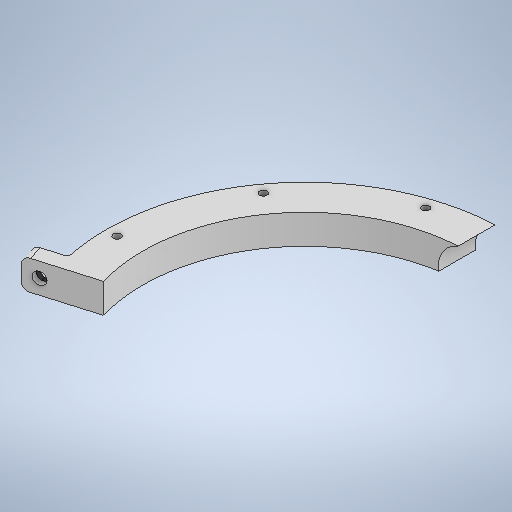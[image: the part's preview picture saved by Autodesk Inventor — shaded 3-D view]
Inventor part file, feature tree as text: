
AUTODESK INVENTOR PART (.ipt)
format: ipt  version: 2025 (Build 290162000, 162)  size: 368,640 bytes
history: native  units: in
note: dims shown in document units (in); Inventor stores cm internally (conversion verified against a paired STEP export)
features: sketch x11, extrude x8, hole x2, projected_geometry x2, fillet x1
ambient origin geometry x8: Origin, YZ Plane, XZ Plane, XY Plane, X Axis, Y Axis, Z Axis, Center Point
bodies: Solid1 (feature_tree)
feature tree (24):
  extrude  "Extrusion1"  Depth=10.6299in
  extrude  "Extrusion2"  Depth=1.4173in
  hole  "Hole1"  [1 undecoded]
  extrude  "Extrusion3"  Depth=0.1575in TaperAngle=360.0deg
  extrude  "Extrusion7"  Depth=0.1575in TaperAngle=0.0deg
  extrude  "Extrusion8"  Depth=2.7559in
  extrude  "Extrusion9"  Depth=0.7874in
  extrude  "Extrusion10"  TaperAngle=0.0deg  [1 undecoded]
  fillet  "Fillet1"  [1 undecoded]
  extrude  "Extrusion11"  Depth=0.7874in
  hole  "Hole2"  [1 undecoded]
  sketch  "Sketch1"  dims[d0=10.6299in d1=8.6614in]
  sketch  "Sketch2"  dims[d5=0.0in d6=0.0in d7=10.0394in]
  sketch  "Sketch3"  dims[d8=0.1575in d9=3.937in d11=360.0deg]
  sketch  "Sketch Circular Pattern1"  dims[d2=1.8504in d3=0.0in d4=1.4173in]
  sketch  "Sketch4"  dims[d13=0.1969in d14=0.3937in d15=0.1575in d16=0.0787in d17=90.0deg d18=0.5591in d19=0.8108in d20=1.063in d21=0.0in]
  sketch  "Sketch7"  dims[d38=0.1181in d39=2.7559in]
  sketch  "Sketch8"  dims[d40=0.7874in d41=7.874in]
  sketch  "Sketch9"  dims[d42=0.5906in d43=0.0in d44=0.0in d45=0.0in d46=0.0in d47=0.0in]
  projected_geometry  "Projected Loop1"
  projected_geometry  "Projected Loop2"
  sketch  "Sketch10"  dims[d48=0.8858in d49=0.7874in]
  sketch  "Sketch11"  dims[d50=0.7874in d51=0.1969in]
  sketch  "Sketch12"  dims[d52=0.3937in d53=0.0in d54=0.0984in d55=0.3937in d56=0.3937in d57=0.5197in d58=0.2362in d59=0.0in d60=0.3937in d61=0.3937in d62=0.3228in d63=0.2362in d64=0.1575in d65=0.0787in d66=90.0deg d67=0.315in d68=0.8108in d30=0.0197in d31=0.0344in d32=0.0197in d33=0.0344in]
note: 4 required parameter values undecoded (feature->parameter linkage not recoverable at this tier; creation-order binding heuristic only, values carry confidence <= 0.55)
